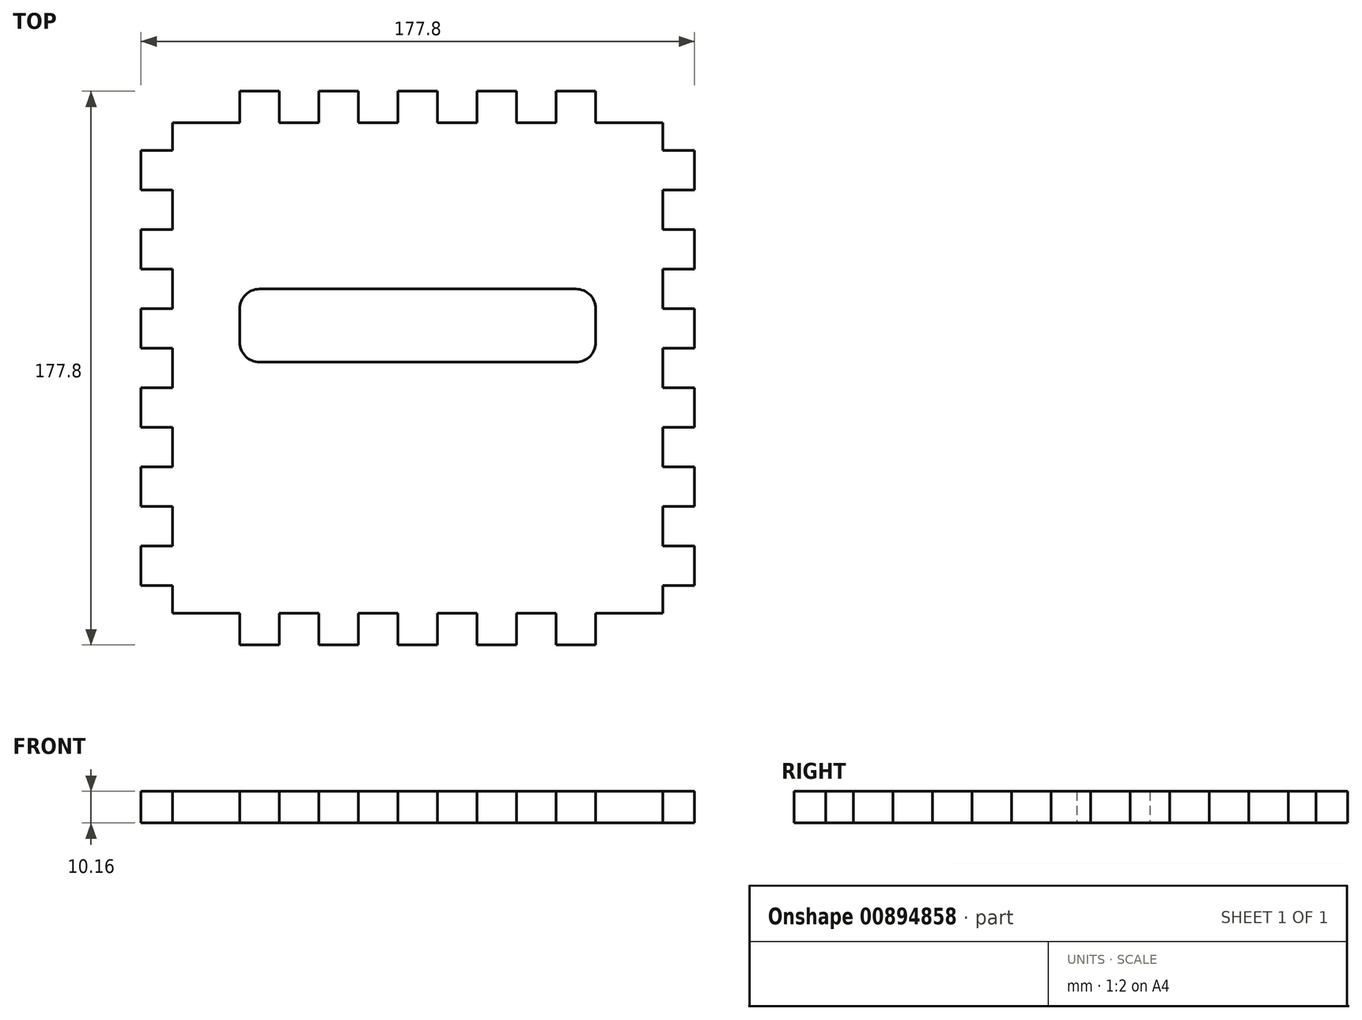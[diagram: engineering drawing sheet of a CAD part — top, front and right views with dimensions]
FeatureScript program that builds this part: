
annotation { "Feature Type Name" : "Feature", "Feature Type Description" : "" }
export const myFeature = defineFeature(function(context is Context, id is Id, definition is map)
    precondition{}
    {
        {
            var Q0;
            Q0=qCreatedBy(makeId("Top.planeOp"),FACE);
            var sketch = newSketch(context, id + "F0", { "sketchPlane" : qUnion([Q0])});
            skLineSegment(sketch, "E0.bottom", {"start": v(31.75, 0) * mm, "end": v(44.45, 0) * mm});
            skLineSegment(sketch, "E0.left", {"start": v(0, -19.05) * mm, "end": v(0, -31.75) * mm});
            skLineSegment(sketch, "E1", {"start": v(10.16, -10.16) * mm, "end": v(31.75, -10.16) * mm});
            skLineSegment(sketch, "E2", {"start": v(31.75, -10.16) * mm, "end": v(31.75, 0) * mm});
            skLineSegment(sketch, "E3", {"start": v(44.45, 0) * mm, "end": v(44.45, -10.16) * mm});
            skLineSegment(sketch, "E4", {"start": v(44.45, -10.16) * mm, "end": v(57.15, -10.16) * mm});
            skLineSegment(sketch, "E5", {"start": v(57.15, -10.16) * mm, "end": v(57.15, 0) * mm});
            skLineSegment(sketch, "E6", {"start": v(57.15, 0) * mm, "end": v(69.85, 0) * mm});
            skLineSegment(sketch, "E7", {"start": v(69.85, 0) * mm, "end": v(69.85, -10.16) * mm});
            skLineSegment(sketch, "E8", {"start": v(69.85, -10.16) * mm, "end": v(82.55, -10.16) * mm});
            skLineSegment(sketch, "E9", {"start": v(82.55, -10.16) * mm, "end": v(82.55, 0) * mm});
            skLineSegment(sketch, "E10", {"start": v(82.55, 0) * mm, "end": v(95.25, 0) * mm});
            skLineSegment(sketch, "E11", {"start": v(95.25, 0) * mm, "end": v(95.25, -10.16) * mm});
            skLineSegment(sketch, "E12", {"start": v(95.25, -10.16) * mm, "end": v(107.95, -10.16) * mm});
            skLineSegment(sketch, "E13", {"start": v(107.95, -10.16) * mm, "end": v(107.95, 0) * mm});
            skLineSegment(sketch, "E14.trimOffspring", {"start": v(107.95, 0) * mm, "end": v(120.65, 0) * mm});
            skPoint(sketch, "E15.orphan", {"position": v(0, 0) * mm});
            skLineSegment(sketch, "E16", {"start": v(120.65, 0) * mm, "end": v(120.65, -10.16) * mm});
            skLineSegment(sketch, "E17", {"start": v(120.65, -10.16) * mm, "end": v(133.35, -10.16) * mm});
            skLineSegment(sketch, "E18", {"start": v(133.35, -10.16) * mm, "end": v(133.35, 0) * mm});
            skLineSegment(sketch, "E19", {"start": v(133.35, 0) * mm, "end": v(146.05, 0) * mm});
            skLineSegment(sketch, "E20", {"start": v(146.05, 0) * mm, "end": v(146.05, -10.16) * mm});
            skLineSegment(sketch, "E21", {"start": v(146.05, -10.16) * mm, "end": v(167.64, -10.16) * mm});
            skPoint(sketch, "E22.orphan", {"position": v(177.8, 0) * mm});
            skLineSegment(sketch, "E23", {"start": v(10.16, -10.16) * mm, "end": v(10.16, -19.05) * mm});
            skLineSegment(sketch, "E24", {"start": v(10.16, -19.05) * mm, "end": v(0, -19.05) * mm});
            skLineSegment(sketch, "E25", {"start": v(0, -31.75) * mm, "end": v(10.16, -31.75) * mm});
            skLineSegment(sketch, "E26", {"start": v(10.16, -31.75) * mm, "end": v(10.16, -44.45) * mm});
            skLineSegment(sketch, "E27", {"start": v(10.16, -44.45) * mm, "end": v(0, -44.45) * mm});
            skLineSegment(sketch, "E28", {"start": v(0, -44.45) * mm, "end": v(0, -57.15) * mm});
            skLineSegment(sketch, "E29", {"start": v(0, -57.15) * mm, "end": v(10.16, -57.15) * mm});
            skLineSegment(sketch, "E30", {"start": v(10.16, -57.15) * mm, "end": v(10.16, -69.85) * mm});
            skLineSegment(sketch, "E31", {"start": v(10.16, -69.85) * mm, "end": v(0, -69.85) * mm});
            skLineSegment(sketch, "E32", {"start": v(0, -69.85) * mm, "end": v(0, -82.55) * mm});
            skLineSegment(sketch, "E33", {"start": v(0, -82.55) * mm, "end": v(10.16, -82.55) * mm});
            skLineSegment(sketch, "E34", {"start": v(10.16, -82.55) * mm, "end": v(10.16, -95.25) * mm});
            skLineSegment(sketch, "E35", {"start": v(10.16, -95.25) * mm, "end": v(0, -95.25) * mm});
            skLineSegment(sketch, "E36.trimOffspring", {"start": v(0, -95.25) * mm, "end": v(0, -107.95) * mm});
            skLineSegment(sketch, "E37", {"start": v(0, -107.95) * mm, "end": v(10.16, -107.95) * mm});
            skLineSegment(sketch, "E38", {"start": v(10.16, -107.95) * mm, "end": v(10.16, -120.65) * mm});
            skLineSegment(sketch, "E39", {"start": v(10.16, -120.65) * mm, "end": v(0, -120.65) * mm});
            skLineSegment(sketch, "E40", {"start": v(0, -120.65) * mm, "end": v(0, -133.35) * mm});
            skLineSegment(sketch, "E41", {"start": v(0, -133.35) * mm, "end": v(10.16, -133.35) * mm});
            skLineSegment(sketch, "E42", {"start": v(10.16, -133.35) * mm, "end": v(10.16, -146.05) * mm});
            skLineSegment(sketch, "E43", {"start": v(10.16, -146.05) * mm, "end": v(0, -146.05) * mm});
            skLineSegment(sketch, "E44.trimOffspring", {"start": v(0, -146.05) * mm, "end": v(0, -158.75) * mm});
            skLineSegment(sketch, "E45", {"start": v(0, -158.75) * mm, "end": v(10.16, -158.75) * mm});
            skLineSegment(sketch, "E46", {"start": v(10.16, -158.75) * mm, "end": v(10.16, -167.64) * mm});
            skLineSegment(sketch, "E47", {"start": v(10.16, -167.64) * mm, "end": v(31.75, -167.64) * mm});
            skLineSegment(sketch, "E48", {"start": v(31.75, -167.64) * mm, "end": v(31.75, -177.8) * mm});
            skPoint(sketch, "E49.orphan", {"position": v(0, -177.8) * mm});
            skLineSegment(sketch, "E50", {"start": v(88.9, 0) * mm, "end": v(88.9, 0) * mm});
            skLineSegment(sketch, "E51", {"start": v(10.16, -88.9) * mm, "end": v(10.16, -88.9) * mm});
            skLineSegment(sketch, "E52.MirrorCS", {"start": v(167.64, -158.75) * mm, "end": v(167.64, -167.64) * mm});
            skLineSegment(sketch, "E53.MirrorCS", {"start": v(167.64, -95.25) * mm, "end": v(177.8, -95.25) * mm});
            skLineSegment(sketch, "E54.MirrorCS", {"start": v(177.8, -57.15) * mm, "end": v(167.64, -57.15) * mm});
            skLineSegment(sketch, "E55.MirrorCS", {"start": v(167.64, -19.05) * mm, "end": v(177.8, -19.05) * mm});
            skLineSegment(sketch, "E56.MirrorCS", {"start": v(167.64, -146.05) * mm, "end": v(177.8, -146.05) * mm});
            skLineSegment(sketch, "E57.MirrorCS", {"start": v(177.8, -82.55) * mm, "end": v(167.64, -82.55) * mm});
            skLineSegment(sketch, "E58.MirrorCS", {"start": v(177.8, -133.35) * mm, "end": v(167.64, -133.35) * mm});
            skLineSegment(sketch, "E59.MirrorCS", {"start": v(167.64, -44.45) * mm, "end": v(177.8, -44.45) * mm});
            skLineSegment(sketch, "E60.MirrorCS", {"start": v(167.64, -69.85) * mm, "end": v(177.8, -69.85) * mm});
            skLineSegment(sketch, "E61.MirrorCS", {"start": v(177.8, -107.95) * mm, "end": v(167.64, -107.95) * mm});
            skLineSegment(sketch, "E62.MirrorCS", {"start": v(177.8, -158.75) * mm, "end": v(167.64, -158.75) * mm});
            skLineSegment(sketch, "E63.MirrorCS", {"start": v(167.64, -10.16) * mm, "end": v(167.64, -19.05) * mm});
            skLineSegment(sketch, "E64.MirrorCS", {"start": v(177.8, -31.75) * mm, "end": v(167.64, -31.75) * mm});
            skLineSegment(sketch, "E65.MirrorCS", {"start": v(167.64, -120.65) * mm, "end": v(177.8, -120.65) * mm});
            skLineSegment(sketch, "E66.MirrorCS", {"start": v(177.8, -19.05) * mm, "end": v(177.8, -31.75) * mm});
            skLineSegment(sketch, "E67.MirrorCS", {"start": v(146.05, -167.64) * mm, "end": v(146.05, -177.8) * mm});
            skLineSegment(sketch, "E68.MirrorCS", {"start": v(167.64, -82.55) * mm, "end": v(167.64, -95.25) * mm});
            skLineSegment(sketch, "E69.MirrorCS", {"start": v(177.8, -44.45) * mm, "end": v(177.8, -57.15) * mm});
            skLineSegment(sketch, "E70.MirrorCS", {"start": v(177.8, -69.85) * mm, "end": v(177.8, -82.55) * mm});
            skLineSegment(sketch, "E71.MirrorCS", {"start": v(177.8, -120.65) * mm, "end": v(177.8, -133.35) * mm});
            skLineSegment(sketch, "E72.MirrorCS", {"start": v(177.8, -95.25) * mm, "end": v(177.8, -107.95) * mm});
            skLineSegment(sketch, "E73.MirrorCS", {"start": v(177.8, -146.05) * mm, "end": v(177.8, -158.75) * mm});
            skLineSegment(sketch, "E74.MirrorCS", {"start": v(167.64, -31.75) * mm, "end": v(167.64, -44.45) * mm});
            skLineSegment(sketch, "E75.MirrorCS", {"start": v(167.64, -10.16) * mm, "end": v(146.05, -10.16) * mm});
            skPoint(sketch, "E76.MirrorP", {"position": v(177.8, -177.8) * mm});
            skLineSegment(sketch, "E77.MirrorCS", {"start": v(167.64, -133.35) * mm, "end": v(167.64, -146.05) * mm});
            skLineSegment(sketch, "E78.MirrorCS", {"start": v(167.64, -107.95) * mm, "end": v(167.64, -120.65) * mm});
            skLineSegment(sketch, "E79.MirrorCS", {"start": v(167.64, -57.15) * mm, "end": v(167.64, -69.85) * mm});
            skLineSegment(sketch, "E80.MirrorCS", {"start": v(167.64, -167.64) * mm, "end": v(146.05, -167.64) * mm});
            skLineSegment(sketch, "E81.MirrorCS", {"start": v(146.05, -167.64) * mm, "end": v(167.64, -167.64) * mm});
            skLineSegment(sketch, "E82.MirrorCS", {"start": v(120.65, -167.64) * mm, "end": v(133.35, -167.64) * mm});
            skLineSegment(sketch, "E83.MirrorCS", {"start": v(95.25, -167.64) * mm, "end": v(107.95, -167.64) * mm});
            skLineSegment(sketch, "E84.MirrorCS", {"start": v(44.45, -167.64) * mm, "end": v(57.15, -167.64) * mm});
            skLineSegment(sketch, "E85.MirrorCS", {"start": v(69.85, -167.64) * mm, "end": v(82.55, -167.64) * mm});
            skLineSegment(sketch, "E86.MirrorCS", {"start": v(31.75, -177.8) * mm, "end": v(44.45, -177.8) * mm});
            skLineSegment(sketch, "E87.MirrorCS", {"start": v(44.45, -177.8) * mm, "end": v(44.45, -167.64) * mm});
            skLineSegment(sketch, "E88.MirrorCS", {"start": v(57.15, -167.64) * mm, "end": v(57.15, -177.8) * mm});
            skLineSegment(sketch, "E89.MirrorCS", {"start": v(57.15, -177.8) * mm, "end": v(69.85, -177.8) * mm});
            skLineSegment(sketch, "E90.MirrorCS", {"start": v(69.85, -177.8) * mm, "end": v(69.85, -167.64) * mm});
            skLineSegment(sketch, "E91.MirrorCS", {"start": v(82.55, -167.64) * mm, "end": v(82.55, -177.8) * mm});
            skLineSegment(sketch, "E92.MirrorCS", {"start": v(82.55, -177.8) * mm, "end": v(95.25, -177.8) * mm});
            skLineSegment(sketch, "E93.MirrorCS", {"start": v(95.25, -177.8) * mm, "end": v(95.25, -167.64) * mm});
            skLineSegment(sketch, "E94.MirrorCS", {"start": v(107.95, -167.64) * mm, "end": v(107.95, -177.8) * mm});
            skLineSegment(sketch, "E95.MirrorCS", {"start": v(107.95, -177.8) * mm, "end": v(120.65, -177.8) * mm});
            skLineSegment(sketch, "E96.MirrorCS", {"start": v(120.65, -177.8) * mm, "end": v(120.65, -167.64) * mm});
            skLineSegment(sketch, "E97.MirrorCS", {"start": v(133.35, -167.64) * mm, "end": v(133.35, -177.8) * mm});
            skLineSegment(sketch, "E98.MirrorCS", {"start": v(133.35, -177.8) * mm, "end": v(146.05, -177.8) * mm});
            skLineSegment(sketch, "E99.bottom", {"start": v(38.1, -63.5) * mm, "end": v(139.7, -63.5) * mm});
            skLineSegment(sketch, "E99.top", {"start": v(38.1, -87) * mm, "end": v(139.7, -87) * mm});
            skLineSegment(sketch, "E99.left", {"start": v(31.75, -69.85) * mm, "end": v(31.75, -80.64) * mm});
            skLineSegment(sketch, "E99.right", {"start": v(146.05, -69.85) * mm, "end": v(146.05, -80.64) * mm});
            skPoint(sketch, "E100.visualSharp", {"position": v(31.75, -63.5) * mm});
            skArc(sketch, "E100.filletArc", {"start": v(38.1, -63.5) * mm, "mid": v(33.6, -65.36) * mm, "end": v(31.75, -69.85) * mm});
            skPoint(sketch, "E101.visualSharp", {"position": v(31.75, -87) * mm});
            skArc(sketch, "E101.filletArc", {"start": v(31.75, -80.64) * mm, "mid": v(33.6, -85.14) * mm, "end": v(38.1, -87) * mm});
            skPoint(sketch, "E102.visualSharp", {"position": v(146.05, -63.5) * mm});
            skArc(sketch, "E102.filletArc", {"start": v(146.05, -69.85) * mm, "mid": v(144.2, -65.36) * mm, "end": v(139.7, -63.5) * mm});
            skPoint(sketch, "E103.visualSharp", {"position": v(146.05, -87) * mm});
            skArc(sketch, "E103.filletArc", {"start": v(139.7, -87) * mm, "mid": v(144.2, -85.14) * mm, "end": v(146.05, -80.64) * mm});
            skPoint(sketch, "E104.start.orphan", {"position": v(88.9, -63.5) * mm});
            skLineSegment(sketch, "E105", {"start": v(88.9, 0) * mm, "end": v(88.9, -63.5) * mm, "construction": true});
            skSolve(sketch);
        }
        {
            var Q0;
            Q0=makeQuery(id+"F0.imprint","IMPRINT",FACE,{"disambiguationData":[TD([[makeQuery(id+"F0.imprint","IMPRINT",EDGE,{"derivedFrom":sQuery(id+"F0.wireOp",EDGE,"E1")}),-1.0]])]});
            extrude(context, id + "F1", {"entities" : qUnion([Q0]), "depth" : 10.16 * mm, "offsetDistance" : 25.4 * mm});
        }
    });
